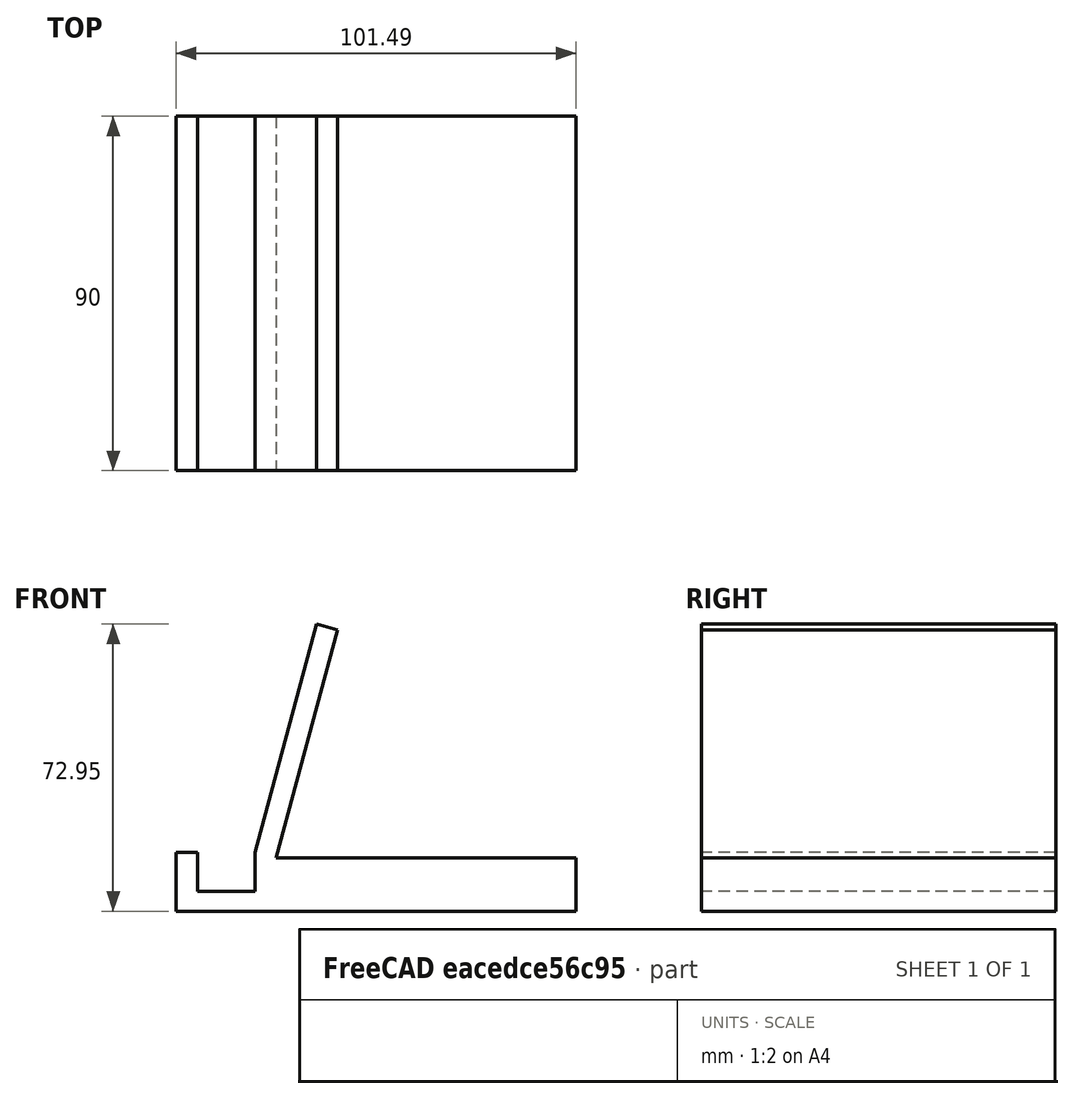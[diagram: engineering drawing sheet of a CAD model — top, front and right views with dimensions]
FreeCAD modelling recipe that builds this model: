
FCSTD DOCUMENT  (FreeCAD 0.16RUnknown)
Label: phone_stand
License: All rights reserved
LicenseURL: http://en.wikipedia.org/wiki/All_rights_reserved
objects: Sketcher::SketchObject×1, PartDesign::Pad×1
note: 3 computed .brp shape members not serialized (recipe doc carries the construction recipe); baked Part::Feature solids carry a one-line shape summary decoded from their .brp

FEATURE [Sketcher::SketchObject] Sketch
  Placement = pos=(0,0,0) rot=(-1,0,0;4.71239rad)
  sketch-geometry (11):
    g0: LineSegment StartX=-39.4626 StartY=5.4785 StartZ=0 EndX=-39.4624 EndY=-9.5215 EndZ=0
    g1: LineSegment StartX=-39.4624 StartY=-9.5215 StartZ=0 EndX=62.0331 EndY=-9.5215 EndZ=0
    g2: LineSegment StartX=62.0331 StartY=-9.5215 StartZ=0 EndX=62.0331 EndY=3.99388 EndZ=0
    g3: LineSegment StartX=62.0331 StartY=3.99388 StartZ=0 EndX=-14.043 EndY=3.99388 EndZ=0
    g4: LineSegment StartX=-14.043 StartY=3.99388 StartZ=0 EndX=1.48618 EndY=61.9494 EndZ=0
    g5: LineSegment StartX=1.48618 StartY=61.9494 StartZ=0 EndX=-3.84301 EndY=63.434 EndZ=0
    g6: LineSegment StartX=-3.84301 StartY=63.434 StartZ=0 EndX=-19.3722 EndY=5.47849 EndZ=0
    g7: LineSegment StartX=-39.4626 StartY=5.4785 StartZ=0 EndX=-34.1013 EndY=5.4785 EndZ=0
    g8: LineSegment StartX=-34.1013 StartY=5.4785 StartZ=0 EndX=-34.1013 EndY=-4.52151 EndZ=0
    g9: LineSegment StartX=-34.1013 StartY=-4.52151 StartZ=0 EndX=-19.3855 EndY=-4.52151 EndZ=0
    g10: LineSegment StartX=-19.3855 StartY=-4.52151 StartZ=0 EndX=-19.3722 EndY=5.47849 EndZ=0
  constraints (23):
    c: Coincident(g0,g1)
    c: Horizontal(g1)
    c: Coincident(g1,g2)
    c: Coincident(g2,g3)
    c: Horizontal(g3)
    c: Coincident(g3,g4)
    c: Coincident(g4,g5)
    c: Coincident(g5,g6)
    c: Distance(g6) = 60
    c: Equal(g4,g6)
    c: Angle(g3,g4) = 1.309
    c: Angle(g3,g6) = 1.309
    c: Coincident(g0,g7)
    c: Coincident(g7,g8)
    c: Coincident(g8,g9)
    c: Coincident(g9,g10)
    c: Coincident(g10,g6)
    c: Equal(g10,g8)
    c: DistanceY(g10,g10) = 10
    c: Parallel(g7,g1)
    c: Parallel(g9,g1)
    c: DistanceY(g0,g0) = 15
    c: Parallel(g3,g1)
FEATURE [PartDesign::Pad] Pad
  Length = 90
  Length2 = 100
  Placement = pos=(0,0,0) rot=(-1,0,0;4.71239rad)
  Sketch = -> Sketch
  Type = 0
